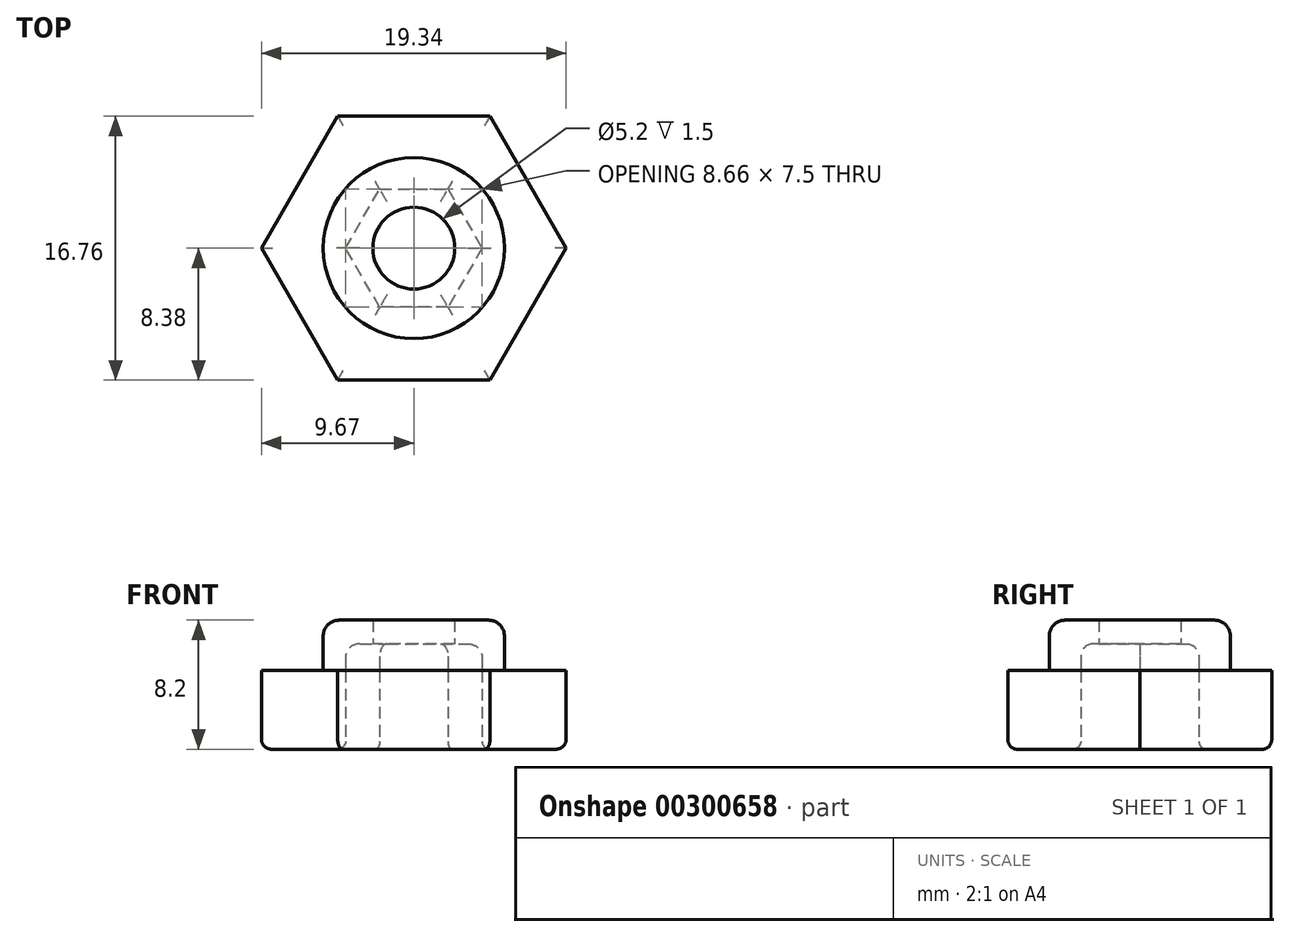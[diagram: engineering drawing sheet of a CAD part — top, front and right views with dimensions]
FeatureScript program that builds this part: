
annotation { "Feature Type Name" : "Feature", "Feature Type Description" : "" }
export const myFeature = defineFeature(function(context is Context, id is Id, definition is map)
    precondition{}
    {
        {
            var Q0;
            Q0=qCreatedBy(makeId("Top.planeOp"),FACE);
            var sketch = newSketch(context, id + "F0", { "sketchPlane" : qUnion([Q0])});
            skCircle(sketch, "E0.cCircle", {"center": v(0, 0) * mm, "radius": 8.38 * mm, "construction": true});
            skLineSegment(sketch, "E0.0", {"start": v(9.67, 0) * mm, "end": v(4.84, -8.38) * mm});
            skLineSegment(sketch, "E0.1", {"start": v(4.84, -8.38) * mm, "end": v(-4.84, -8.37) * mm});
            skLineSegment(sketch, "E0.2", {"start": v(-4.84, -8.38) * mm, "end": v(-9.67, 0) * mm});
            skLineSegment(sketch, "E0.3", {"start": v(-9.67, 0) * mm, "end": v(-4.84, 8.38) * mm});
            skLineSegment(sketch, "E0.4", {"start": v(-4.84, 8.37) * mm, "end": v(4.84, 8.37) * mm});
            skLineSegment(sketch, "E0.5", {"start": v(4.84, 8.38) * mm, "end": v(9.67, 0) * mm});
            skPoint(sketch, "E0.0.midPoint", {"position": v(7.25, -4.19) * mm});
            skCircle(sketch, "E1.cCircle", {"center": v(0, 0) * mm, "radius": 3.75 * mm, "construction": true});
            skLineSegment(sketch, "E1.0", {"start": v(4.33, 0) * mm, "end": v(2.17, -3.75) * mm});
            skLineSegment(sketch, "E1.1", {"start": v(2.17, -3.75) * mm, "end": v(-2.17, -3.75) * mm});
            skLineSegment(sketch, "E1.2", {"start": v(-2.17, -3.75) * mm, "end": v(-4.33, 0) * mm});
            skLineSegment(sketch, "E1.3", {"start": v(-4.33, 0) * mm, "end": v(-2.17, 3.75) * mm});
            skLineSegment(sketch, "E1.4", {"start": v(-2.17, 3.75) * mm, "end": v(2.17, 3.75) * mm});
            skLineSegment(sketch, "E1.5", {"start": v(2.17, 3.75) * mm, "end": v(4.33, 0) * mm});
            skPoint(sketch, "E1.0.midPoint", {"position": v(3.25, -1.88) * mm});
            skSolve(sketch);
        }
        {
            var Q0;
            Q0=makeQuery(id+"F0.imprint","IMPRINT",FACE,{"disambiguationData":[TD([[makeQuery(id+"F0.imprint","IMPRINT",EDGE,{"derivedFrom":sQuery(id+"F0.wireOp",EDGE,"E0.0")}),-1.0]])]});
            extrude(context, id + "F1", {"entities" : qUnion([Q0]), "depth" : 5 * mm});
        }
        {
            var Q0;
            Q0=makeQuery(id+"F1.opExtrude","CAP_FACE",FACE,{"disambiguationData":[OSD([sQuery(id+"F0.wireOp",EDGE,"E0.0"),sQuery(id+"F0.wireOp",EDGE,"E0.1"),sQuery(id+"F0.wireOp",EDGE,"E0.2"),sQuery(id+"F0.wireOp",EDGE,"E0.3"),sQuery(id+"F0.wireOp",EDGE,"E0.4"),sQuery(id+"F0.wireOp",EDGE,"E0.5"),sQuery(id+"F0.wireOp",EDGE,"E1.0"),sQuery(id+"F0.wireOp",EDGE,"E1.1"),sQuery(id+"F0.wireOp",EDGE,"E1.2"),sQuery(id+"F0.wireOp",EDGE,"E1.3"),sQuery(id+"F0.wireOp",EDGE,"E1.4"),sQuery(id+"F0.wireOp",EDGE,"E1.5")])],"isStart":false});
            var sketch = newSketch(context, id + "F2", { "sketchPlane" : qUnion([Q0])});
            skCircle(sketch, "E2", {"center": v(0, 0) * mm, "radius": 5.75 * mm});
            skSolve(sketch);
        }
        {
            var Q0;
            Q0=makeQuery(id+"F2.imprint","IMPRINT",FACE,{"disambiguationData":[TD([[makeQuery(id+"F2.imprint","IMPRINT",EDGE,{"derivedFrom":sQuery(id+"F2.wireOp",EDGE,"E2")}),1.0]])]});
            var Q1;
            Q1=sQuery(id+"F2.wireOp",EDGE,"E2");
            extrude(context, id + "F3", {"entities" : qUnion([Q0]), "surfaceEntities" : qUnion([Q1]), "offsetDistance" : 25 * mm, "depth" : 1.2 * mm});
        }
        {
            var Q0;
            Q0=makeQuery(id+"F3.opExtrude","CAP_FACE",FACE,{"disambiguationData":[OSD([sQuery(id+"F0.wireOp",EDGE,"E1.0"),sQuery(id+"F0.wireOp",EDGE,"E1.1"),sQuery(id+"F0.wireOp",EDGE,"E1.2"),sQuery(id+"F0.wireOp",EDGE,"E1.3"),sQuery(id+"F0.wireOp",EDGE,"E1.4"),sQuery(id+"F0.wireOp",EDGE,"E1.5"),sQuery(id+"F2.wireOp",EDGE,"E2")])],"isStart":false});
            var sketch = newSketch(context, id + "F4", { "sketchPlane" : qUnion([Q0])});
            skCircle(sketch, "E3", {"center": v(0, 0) * mm, "radius": 2.6 * mm});
            skSolve(sketch);
        }
        {
            var Q0;
            Q0=makeQuery(id+"F4.imprint","IMPRINT",FACE,{"disambiguationData":[TD([[makeQuery(id+"F4.imprint","IMPRINT",EDGE,{"derivedFrom":makeQuery(id+"F3.opExtrude","CAP_EDGE",EDGE,{"disambiguationData":[OSD([sQuery(id+"F2.wireOp",EDGE,"E2")])],"isStart":false})}),1.0]])]});
            var Q1;
            Q1=makeQuery(id+"F4.imprint","IMPRINT",FACE,{"disambiguationData":[TD([[makeQuery(id+"F4.imprint","IMPRINT",EDGE,{"derivedFrom":sQuery(id+"F4.wireOp",EDGE,"E3")}),-1.0]])]});
            extrude(context, id + "F5", {"entities" : qUnion([Q0, Q1]), "operationType" : NewBodyOperationType.ADD, "depth" : 2 * mm, "offsetDistance" : 25 * mm});
        }
        {
            var Q0;
            Q0=makeQuery(id+"F1.opExtrude","SWEPT_FACE",FACE,{"disambiguationData":[OSD([sQuery(id+"F0.wireOp",EDGE,"E1.5")])]});
            var Q1;
            {var subQ0=sQuery(id+"F0.wireOp",EDGE,"E1.3");var subQ1=sQuery(id+"F0.wireOp",EDGE,"E1.1");var subQ3=sQuery(id+"F0.wireOp",EDGE,"E1.2");Q1=makeQuery(id+"FvVf4zqVTHiOcPK_2.boolean.opBoolean","SPLIT",FACE,{"disambiguationData":[TD([makeQuery(id+"F1.opExtrude","CAP_FACE",FACE,{"disambiguationData":[OSD([sQuery(id+"F0.wireOp",EDGE,"E0.0"),sQuery(id+"F0.wireOp",EDGE,"E0.1"),sQuery(id+"F0.wireOp",EDGE,"E0.2"),sQuery(id+"F0.wireOp",EDGE,"E0.3"),sQuery(id+"F0.wireOp",EDGE,"E0.4"),sQuery(id+"F0.wireOp",EDGE,"E0.5"),sQuery(id+"F0.wireOp",EDGE,"E1.0"),subQ1,subQ3,subQ0,sQuery(id+"F0.wireOp",EDGE,"E1.4"),sQuery(id+"F0.wireOp",EDGE,"E1.5")])],"isStart":false})])],"derivedFrom":makeQuery(id+"F1.opExtrude","SWEPT_FACE",FACE,{"disambiguationData":[OSD([subQ3])]})});}
            cPlane(context, id + "F6", {"entities" : qUnion([Q0, Q1]), "cplaneType" : CPlaneType.MID_PLANE, "offset" : 25 * mm, "width" : 150 * mm, "height" : 150 * mm});
        }
        {
            var Q0;
            Q0=makeQuery(id+"F5.opExtrude","CAP_EDGE",EDGE,{"disambiguationData":[OSD([sQuery(id+"F2.wireOp",EDGE,"E2")])],"isStart":false});
            fillet(context, id + "F7", {"entities" : qUnion([Q0]), "radius" : 1 * mm, "tangentPropagation" : true, "allowEdgeOverflow" : false});
        }
        {
            var Q0;
            Q0=makeQuery(id+"F1.opExtrude","CAP_EDGE",EDGE,{"disambiguationData":[OSD([sQuery(id+"F0.wireOp",EDGE,"E0.2")])],"isStart":true});
            var Q1;
            Q1=makeQuery(id+"F1.opExtrude","CAP_EDGE",EDGE,{"disambiguationData":[OSD([sQuery(id+"F0.wireOp",EDGE,"E0.3")])],"isStart":true});
            var Q2;
            Q2=makeQuery(id+"F1.opExtrude","CAP_EDGE",EDGE,{"disambiguationData":[OSD([sQuery(id+"F0.wireOp",EDGE,"E0.4")])],"isStart":true});
            var Q3;
            Q3=makeQuery(id+"F1.opExtrude","CAP_EDGE",EDGE,{"disambiguationData":[OSD([sQuery(id+"F0.wireOp",EDGE,"E0.5")])],"isStart":true});
            var Q4;
            Q4=makeQuery(id+"F1.opExtrude","CAP_EDGE",EDGE,{"disambiguationData":[OSD([sQuery(id+"F0.wireOp",EDGE,"E0.0")])],"isStart":true});
            var Q5;
            Q5=makeQuery(id+"F1.opExtrude","CAP_EDGE",EDGE,{"disambiguationData":[OSD([sQuery(id+"F0.wireOp",EDGE,"E0.1")])],"isStart":true});
            fillet(context, id + "F8", {"entities" : qUnion([Q0, Q1, Q2, Q3, Q4, Q5]), "radius" : 0.6 * mm, "tangentPropagation" : true, "allowEdgeOverflow" : false});
        }
        {
            var Q0;
            Q0=makeQuery(id+"F5.opExtrude","CAP_FACE",FACE,{"disambiguationData":[OSD([sQuery(id+"F2.wireOp",EDGE,"E2"),sQuery(id+"F4.wireOp",EDGE,"E3")])],"isStart":true});
            extrude(context, id + "F9", {"entities" : qUnion([Q0]), "operationType" : NewBodyOperationType.REMOVE, "oppositeDirection" : true, "depth" : 0.5 * mm, "offsetDistance" : 25 * mm});
        }
        {
            var Q0;
            Q0=makeQuery(id+"F9.boolean.opBoolean","COPY",EDGE,{"derivedFrom":makeQuery(id+"F9.opExtrude","CAP_EDGE",EDGE,{"disambiguationData":[OSD([sQuery(id+"F0.wireOp",EDGE,"E1.0")])],"isStart":false})});
            var Q1;
            Q1=makeQuery(id+"F9.boolean.opBoolean","COPY",EDGE,{"derivedFrom":makeQuery(id+"F9.opExtrude","CAP_EDGE",EDGE,{"disambiguationData":[OSD([sQuery(id+"F0.wireOp",EDGE,"E1.5")])],"isStart":false})});
            var Q2;
            Q2=makeQuery(id+"F9.boolean.opBoolean","COPY",EDGE,{"derivedFrom":makeQuery(id+"F9.opExtrude","CAP_EDGE",EDGE,{"disambiguationData":[OSD([sQuery(id+"F0.wireOp",EDGE,"E1.1")])],"isStart":false})});
            var Q3;
            Q3=makeQuery(id+"F9.boolean.opBoolean","COPY",EDGE,{"derivedFrom":makeQuery(id+"F9.opExtrude","CAP_EDGE",EDGE,{"disambiguationData":[OSD([sQuery(id+"F0.wireOp",EDGE,"E1.2")])],"isStart":false})});
            var Q4;
            Q4=makeQuery(id+"F9.boolean.opBoolean","COPY",EDGE,{"derivedFrom":makeQuery(id+"F9.opExtrude","CAP_EDGE",EDGE,{"disambiguationData":[OSD([sQuery(id+"F0.wireOp",EDGE,"E1.3")])],"isStart":false})});
            var Q5;
            Q5=makeQuery(id+"F9.boolean.opBoolean","COPY",EDGE,{"derivedFrom":makeQuery(id+"F9.opExtrude","CAP_EDGE",EDGE,{"disambiguationData":[OSD([sQuery(id+"F0.wireOp",EDGE,"E1.4")])],"isStart":false})});
            fillet(context, id + "F10", {"entities" : qUnion([Q0, Q1, Q2, Q3, Q4, Q5]), "radius" : 0.8 * mm, "tangentPropagation" : true, "allowEdgeOverflow" : false});
        }
        {
            var Q0;
            Q0=makeQuery(id+"F1.opExtrude","CAP_EDGE",EDGE,{"disambiguationData":[OSD([sQuery(id+"F0.wireOp",EDGE,"E1.0")])],"isStart":true});
            var Q1;
            Q1=makeQuery(id+"F1.opExtrude","CAP_EDGE",EDGE,{"disambiguationData":[OSD([sQuery(id+"F0.wireOp",EDGE,"E1.5")])],"isStart":true});
            var Q2;
            Q2=makeQuery(id+"F1.opExtrude","CAP_EDGE",EDGE,{"disambiguationData":[OSD([sQuery(id+"F0.wireOp",EDGE,"E1.4")])],"isStart":true});
            var Q3;
            Q3=makeQuery(id+"F1.opExtrude","CAP_EDGE",EDGE,{"disambiguationData":[OSD([sQuery(id+"F0.wireOp",EDGE,"E1.3")])],"isStart":true});
            var Q4;
            Q4=makeQuery(id+"F1.opExtrude","CAP_EDGE",EDGE,{"disambiguationData":[OSD([sQuery(id+"F0.wireOp",EDGE,"E1.1")])],"isStart":true});
            var Q5;
            Q5=makeQuery(id+"F1.opExtrude","CAP_EDGE",EDGE,{"disambiguationData":[OSD([sQuery(id+"F0.wireOp",EDGE,"E1.2")])],"isStart":true});
            fillet(context, id + "F11", {"entities" : qUnion([Q0, Q1, Q2, Q3, Q4, Q5]), "radius" : 0.5 * mm, "tangentPropagation" : true, "allowEdgeOverflow" : false});
        }
    });
